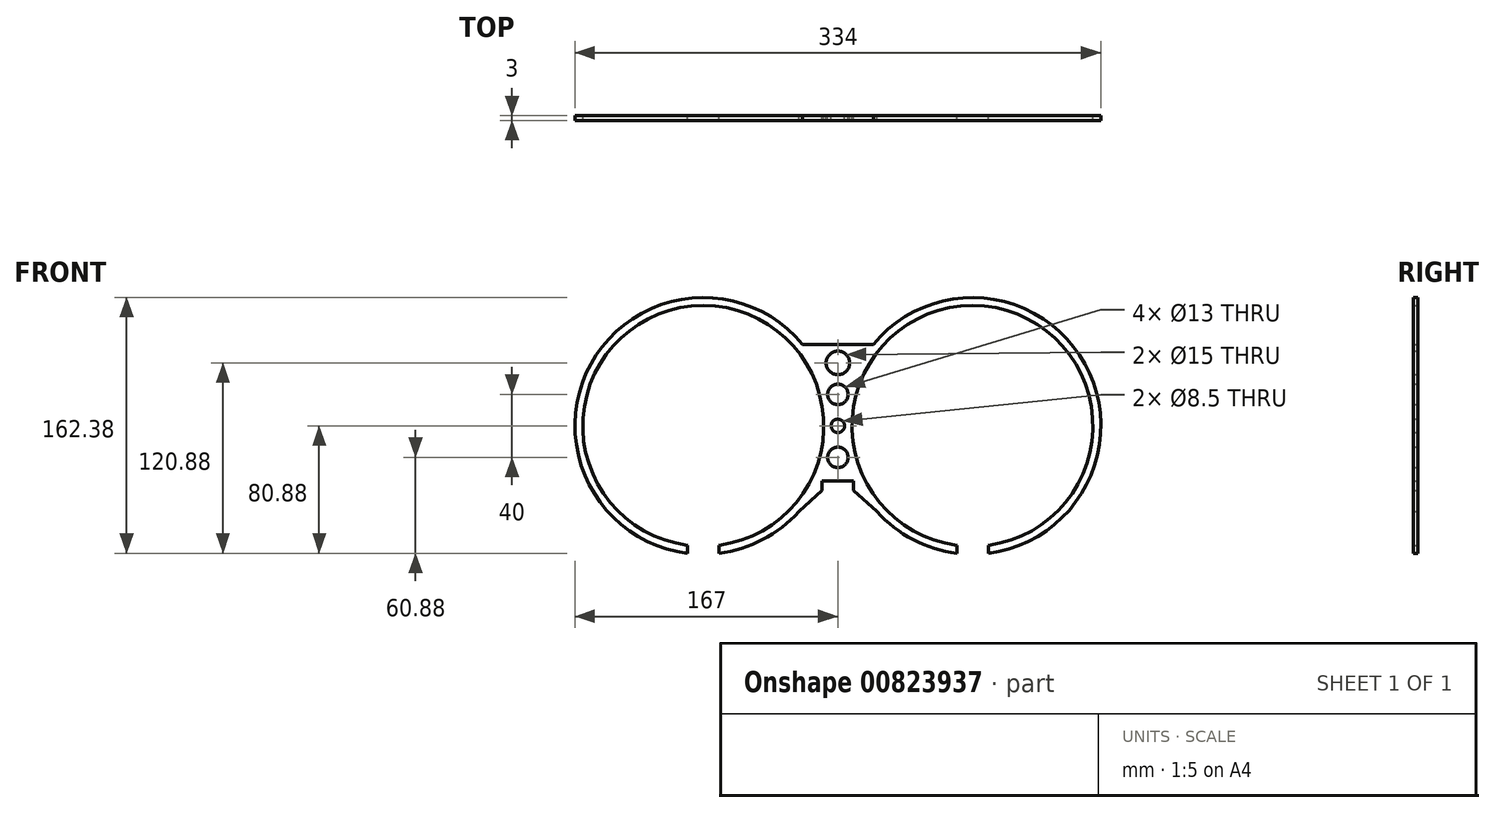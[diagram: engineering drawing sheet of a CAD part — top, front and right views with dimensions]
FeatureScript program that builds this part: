
annotation { "Feature Type Name" : "Feature", "Feature Type Description" : "" }
export const myFeature = defineFeature(function(context is Context, id is Id, definition is map)
    precondition{}
    {
        {
            var Q0;
            Q0=qCreatedBy(makeId("Front.planeOp"),FACE);
            var sketch = newSketch(context, id + "F0", { "sketchPlane" : qUnion([Q0])});
            skArc(sketch, "E0", {"start": v(-75.5, -75.84) * mm, "mid": v(-85.5, 76.5) * mm, "end": v(-95.5, -75.84) * mm});
            skArc(sketch, "E1", {"start": v(-22.5, 51.7) * mm, "mid": v(-156.9, 39.3) * mm, "end": v(-95.5, -80.88) * mm});
            skArc(sketch, "E2", {"start": v(24.83, -54.42) * mm, "mid": v(47.77, -72.24) * mm, "end": v(75.5, -80.88) * mm});
            skArc(sketch, "E3", {"start": v(95.5, -75.84) * mm, "mid": v(85.5, 76.5) * mm, "end": v(75.5, -75.84) * mm});
            skLineSegment(sketch, "E4", {"start": v(-22.5, 51.7) * mm, "end": v(22.5, 51.7) * mm});
            skLineSegment(sketch, "E5", {"start": v(-10, -41) * mm, "end": v(-10, -35) * mm});
            skLineSegment(sketch, "E6", {"start": v(-10, -35) * mm, "end": v(10, -35) * mm});
            skLineSegment(sketch, "E7", {"start": v(10, -35) * mm, "end": v(10, -41) * mm});
            skLineSegment(sketch, "E8", {"start": v(-24.83, -54.42) * mm, "end": v(-10, -41) * mm});
            skLineSegment(sketch, "E9", {"start": v(24.83, -54.42) * mm, "end": v(10, -41) * mm});
            skCircle(sketch, "E10", {"center": v(0, 0) * mm, "radius": 4.25 * mm});
            skCircle(sketch, "E11", {"center": v(0, 20) * mm, "radius": 6.5 * mm});
            skCircle(sketch, "E12", {"center": v(0, 40) * mm, "radius": 7.5 * mm});
            skCircle(sketch, "E13", {"center": v(0, -20) * mm, "radius": 6.5 * mm});
            skLineSegment(sketch, "E14.left", {"start": v(-95.5, -75.84) * mm, "end": v(-95.5, -80.88) * mm});
            skLineSegment(sketch, "E14.right", {"start": v(-75.5, -75.84) * mm, "end": v(-75.5, -80.88) * mm});
            skLineSegment(sketch, "E15.left", {"start": v(75.5, -75.84) * mm, "end": v(75.5, -80.88) * mm});
            skLineSegment(sketch, "E15.right", {"start": v(95.5, -75.84) * mm, "end": v(95.5, -80.88) * mm});
            skArc(sketch, "E16.trimOffspring", {"start": v(95.5, -80.88) * mm, "mid": v(156.9, 39.3) * mm, "end": v(22.5, 51.7) * mm});
            skArc(sketch, "E17.trimOffspring", {"start": v(-75.5, -80.88) * mm, "mid": v(-47.77, -72.24) * mm, "end": v(-24.83, -54.42) * mm});
            skSolve(sketch);
        }
        {
            var Q0;
            Q0=makeQuery(id+"F0.imprint","IMPRINT",FACE,{"disambiguationData":[TD([[makeQuery(id+"F0.imprint","IMPRINT",EDGE,{"derivedFrom":sQuery(id+"F0.wireOp",EDGE,"E0")}),-1.0]])]});
            extrude(context, id + "F1", {"entities" : qUnion([Q0]), "depth" : 3 * mm, "offsetDistance" : 25 * mm});
        }
    });
